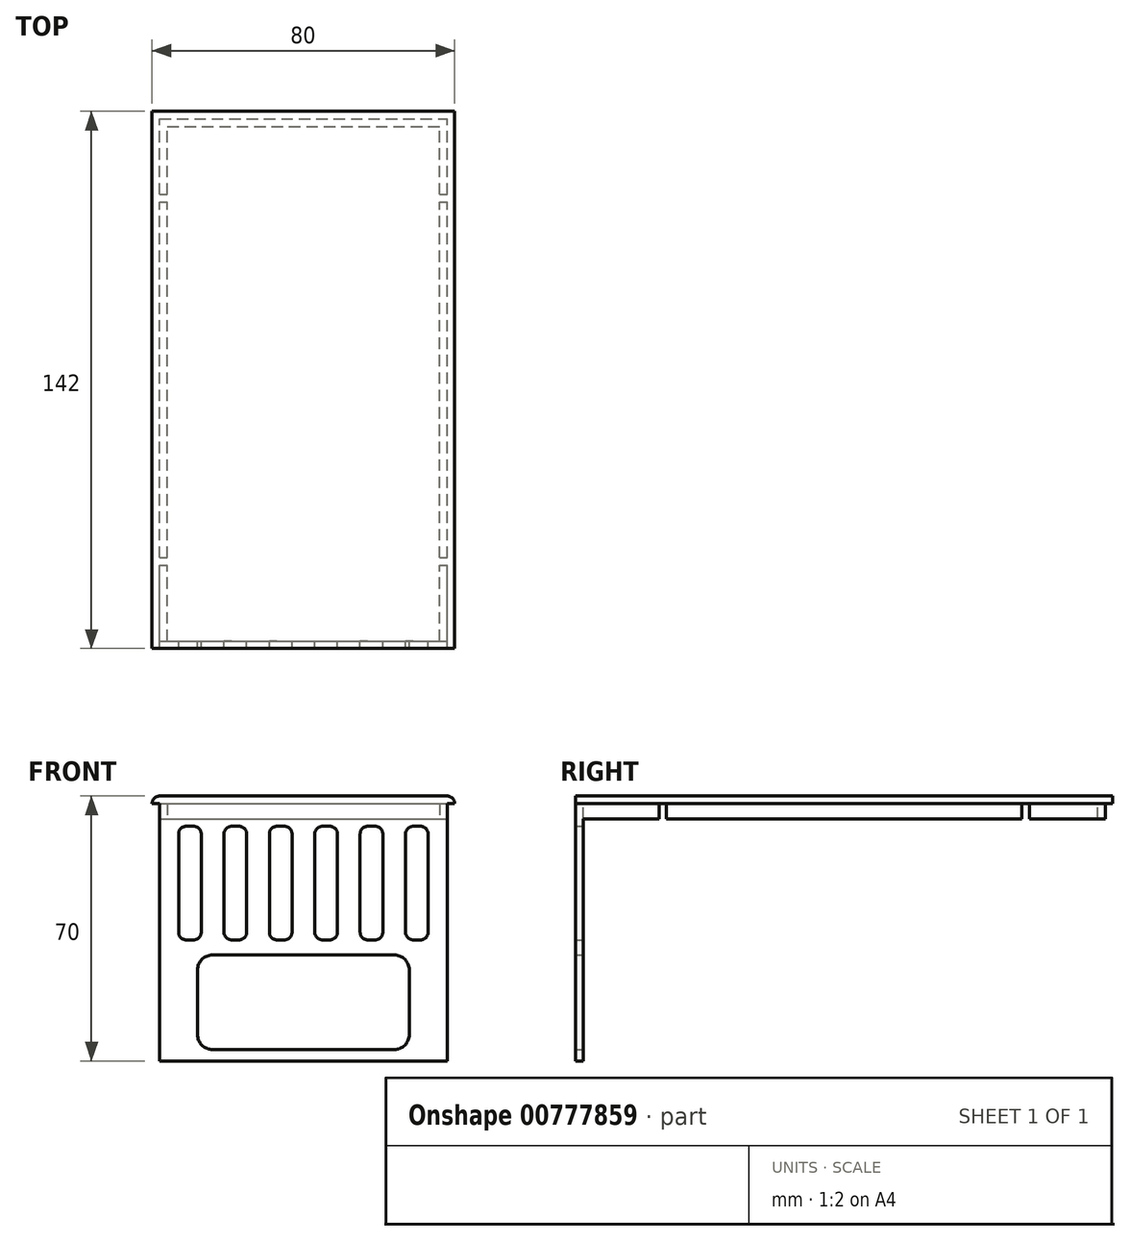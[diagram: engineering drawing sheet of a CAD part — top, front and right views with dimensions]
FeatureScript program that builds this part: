
annotation { "Feature Type Name" : "Feature", "Feature Type Description" : "" }
export const myFeature = defineFeature(function(context is Context, id is Id, definition is map)
    precondition{}
    {
        {
            var Q0;
            Q0=qCreatedBy(makeId("Front.planeOp"),FACE);
            var sketch = newSketch(context, id + "F0", { "sketchPlane" : qUnion([Q0])});
            skLineSegment(sketch, "E0.bottom", {"start": v(-40, -35) * mm, "end": v(36, -35) * mm});
            skLineSegment(sketch, "E0.top", {"start": v(-40, 33) * mm, "end": v(36, 33) * mm});
            skLineSegment(sketch, "E0.left", {"start": v(-40, -35) * mm, "end": v(-40, 33) * mm});
            skLineSegment(sketch, "E0.right", {"start": v(36, -35) * mm, "end": v(36, 33) * mm});
            skPoint(sketch, "E0.middle", {"position": v(-2, -1) * mm});
            skLineSegment(sketch, "E1.bottom", {"start": v(-30, -32) * mm, "end": v(26, -32) * mm});
            skLineSegment(sketch, "E1.top", {"start": v(-30, -7) * mm, "end": v(26, -7) * mm});
            skLineSegment(sketch, "E1.left", {"start": v(-30, -32) * mm, "end": v(-30, -7) * mm});
            skLineSegment(sketch, "E1.right", {"start": v(26, -32) * mm, "end": v(26, -7) * mm});
            skLineSegment(sketch, "E2.bottom", {"start": v(-35, -3) * mm, "end": v(-29, -3) * mm});
            skLineSegment(sketch, "E2.top", {"start": v(-35, 27) * mm, "end": v(-29, 27) * mm});
            skLineSegment(sketch, "E2.left", {"start": v(-35, -3) * mm, "end": v(-35, 27) * mm});
            skLineSegment(sketch, "E2.right", {"start": v(31, -3) * mm, "end": v(31, 27) * mm});
            skLineSegment(sketch, "E3", {"start": v(-29, 27) * mm, "end": v(-29, -3) * mm});
            skLineSegment(sketch, "E4", {"start": v(-23, 27) * mm, "end": v(-23, -3) * mm});
            skLineSegment(sketch, "E5", {"start": v(-17, 27) * mm, "end": v(-17, -3) * mm});
            skLineSegment(sketch, "E6", {"start": v(-11, 27) * mm, "end": v(-11, -3) * mm});
            skLineSegment(sketch, "E7", {"start": v(-5, 27) * mm, "end": v(-5, -3) * mm});
            skLineSegment(sketch, "E8", {"start": v(1, 27) * mm, "end": v(1, -3) * mm});
            skLineSegment(sketch, "E9", {"start": v(7, 27) * mm, "end": v(7, -3) * mm});
            skLineSegment(sketch, "E10", {"start": v(13, 27) * mm, "end": v(13, -3) * mm});
            skLineSegment(sketch, "E11", {"start": v(19, 27) * mm, "end": v(19, -3) * mm});
            skLineSegment(sketch, "E12", {"start": v(25, 27) * mm, "end": v(25, -3) * mm});
            skLineSegment(sketch, "E13", {"start": v(31, 27) * mm, "end": v(31, -3) * mm});
            skLineSegment(sketch, "E14.trimOffspring", {"start": v(-23, 27) * mm, "end": v(-17, 27) * mm});
            skLineSegment(sketch, "E15.trimOffspring", {"start": v(-23, -3) * mm, "end": v(-17, -3) * mm});
            skLineSegment(sketch, "E16.trimOffspring", {"start": v(-11, 27) * mm, "end": v(-5, 27) * mm});
            skLineSegment(sketch, "E17.trimOffspring", {"start": v(-11, -3) * mm, "end": v(-5, -3) * mm});
            skLineSegment(sketch, "E18.trimOffspring", {"start": v(1, -3) * mm, "end": v(7, -3) * mm});
            skLineSegment(sketch, "E19.trimOffspring", {"start": v(1, 27) * mm, "end": v(7, 27) * mm});
            skLineSegment(sketch, "E20.trimOffspring", {"start": v(13, 27) * mm, "end": v(19, 27) * mm});
            skLineSegment(sketch, "E21.trimOffspring", {"start": v(13, -3) * mm, "end": v(19, -3) * mm});
            skLineSegment(sketch, "E22.trimOffspring", {"start": v(25, 27) * mm, "end": v(31, 27) * mm});
            skLineSegment(sketch, "E23.trimOffspring", {"start": v(25, -3) * mm, "end": v(31, -3) * mm});
            skSolve(sketch);
        }
        {
            var Q0;
            Q0=makeQuery(id+"F0.imprint","IMPRINT",FACE,{"disambiguationData":[TD([[makeQuery(id+"F0.imprint","IMPRINT",EDGE,{"derivedFrom":sQuery(id+"F0.wireOp",EDGE,"E0.bottom")}),1.0]])]});
            extrude(context, id + "F1", {"entities" : qUnion([Q0]), "depth" : 2 * mm, "offsetDistance" : 25 * mm});
        }
        {
            var Q0;
            Q0=makeQuery(id+"F1.opExtrude","SWEPT_FACE",FACE,{"disambiguationData":[OSD([sQuery(id+"F0.wireOp",EDGE,"E0.top")])]});
            var sketch = newSketch(context, id + "F2", { "sketchPlane" : qUnion([Q0])});
            skLineSegment(sketch, "E24.bottom", {"start": v(-42, -2) * mm, "end": v(38, -2) * mm});
            skLineSegment(sketch, "E24.top", {"start": v(-42, 140) * mm, "end": v(38, 140) * mm});
            skLineSegment(sketch, "E24.left", {"start": v(-42, -2) * mm, "end": v(-42, 140) * mm});
            skLineSegment(sketch, "E24.right", {"start": v(38, -2) * mm, "end": v(38, 140) * mm});
            skSolve(sketch);
        }
        {
            var Q0;
            Q0 = qSketchRegion(id + "F2", true);
            extrude(context, id + "F3", {"entities" : qUnion([Q0]), "operationType" : NewBodyOperationType.ADD, "depth" : 2 * mm, "offsetDistance" : 25 * mm});
        }
        {
            var Q0;
            Q0=makeQuery(id+"F3.opExtrude","CAP_EDGE",EDGE,{"disambiguationData":[OSD([sQuery(id+"F2.wireOp",EDGE,"E24.right")])],"isStart":false});
            var Q1;
            Q1=makeQuery(id+"F3.opExtrude","CAP_EDGE",EDGE,{"disambiguationData":[OSD([sQuery(id+"F2.wireOp",EDGE,"E24.left")])],"isStart":false});
            fillet(context, id + "F4", {"entities" : qUnion([Q0, Q1]), "radius" : 2 * mm, "tangentPropagation" : true, "allowEdgeOverflow" : false});
        }
        {
            var Q0;
            Q0=makeQuery(id+"F3.opExtrude","CAP_FACE",FACE,{"disambiguationData":[OSD([sQuery(id+"F2.wireOp",EDGE,"E24.bottom"),sQuery(id+"F2.wireOp",EDGE,"E24.top"),sQuery(id+"F2.wireOp",EDGE,"E24.left"),sQuery(id+"F2.wireOp",EDGE,"E24.right")])],"isStart":true});
            var sketch = newSketch(context, id + "F5", { "sketchPlane" : qUnion([Q0])});
            skLineSegment(sketch, "E25.bottom", {"start": v(-40, 0) * mm, "end": v(36, 0) * mm});
            skLineSegment(sketch, "E25.top", {"start": v(-40, -138) * mm, "end": v(36, -138) * mm});
            skLineSegment(sketch, "E25.left", {"start": v(-40, 0) * mm, "end": v(-40, -138) * mm});
            skLineSegment(sketch, "E25.right", {"start": v(36, 0) * mm, "end": v(36, -138) * mm});
            skLineSegment(sketch, "E26.bottom", {"start": v(-38, 0) * mm, "end": v(34, 0) * mm});
            skLineSegment(sketch, "E26.top", {"start": v(-38, -136) * mm, "end": v(34, -136) * mm});
            skLineSegment(sketch, "E26.left", {"start": v(-38, 0) * mm, "end": v(-38, -136) * mm});
            skLineSegment(sketch, "E26.right", {"start": v(34, 0) * mm, "end": v(34, -136) * mm});
            skSolve(sketch);
        }
        {
            var Q0;
            Q0=makeQuery(id+"F5.imprint","IMPRINT",FACE,{"disambiguationData":[TD([[makeQuery(id+"F5.imprint","IMPRINT",EDGE,{"derivedFrom":sQuery(id+"F5.wireOp",EDGE,"E25.top")}),1.0]])]});
            extrude(context, id + "F6", {"entities" : qUnion([Q0]), "operationType" : NewBodyOperationType.ADD, "depth" : 4 * mm, "offsetDistance" : 25 * mm});
        }
        {
            var Q0;
            Q0=makeQuery(id+"F1.opExtrude","SWEPT_EDGE",EDGE,{"disambiguationData":[OSD([sQuery(id+"F0.wireOp",EDGE,"E1.top"),sQuery(id+"F0.wireOp",EDGE,"E1.left")])]});
            var Q1;
            Q1=makeQuery(id+"F1.opExtrude","SWEPT_EDGE",EDGE,{"disambiguationData":[OSD([sQuery(id+"F0.wireOp",EDGE,"E1.top"),sQuery(id+"F0.wireOp",EDGE,"E1.right")])]});
            var Q2;
            Q2=makeQuery(id+"F1.opExtrude","SWEPT_EDGE",EDGE,{"disambiguationData":[OSD([sQuery(id+"F0.wireOp",EDGE,"E1.bottom"),sQuery(id+"F0.wireOp",EDGE,"E1.left")])]});
            var Q3;
            Q3=makeQuery(id+"F1.opExtrude","SWEPT_EDGE",EDGE,{"disambiguationData":[OSD([sQuery(id+"F0.wireOp",EDGE,"E1.bottom"),sQuery(id+"F0.wireOp",EDGE,"E1.right")])]});
            fillet(context, id + "F7", {"entities" : qUnion([Q0, Q1, Q2, Q3]), "radius" : 4 * mm, "tangentPropagation" : true, "allowEdgeOverflow" : false});
        }
        {
            var Q0;
            Q0=makeQuery(id+"F1.opExtrude","SWEPT_EDGE",EDGE,{"disambiguationData":[OSD([sQuery(id+"F0.wireOp",EDGE,"E2.top"),sQuery(id+"F0.wireOp",EDGE,"E2.left")])]});
            var Q1;
            Q1=makeQuery(id+"F1.opExtrude","SWEPT_EDGE",EDGE,{"disambiguationData":[OSD([sQuery(id+"F0.wireOp",EDGE,"E2.top"),sQuery(id+"F0.wireOp",EDGE,"E3")])]});
            var Q2;
            Q2=makeQuery(id+"F1.opExtrude","SWEPT_EDGE",EDGE,{"disambiguationData":[OSD([sQuery(id+"F0.wireOp",EDGE,"E2.bottom"),sQuery(id+"F0.wireOp",EDGE,"E2.left")])]});
            var Q3;
            Q3=makeQuery(id+"F1.opExtrude","SWEPT_EDGE",EDGE,{"disambiguationData":[OSD([sQuery(id+"F0.wireOp",EDGE,"E2.bottom"),sQuery(id+"F0.wireOp",EDGE,"E3")])]});
            var Q4;
            Q4=makeQuery(id+"F1.opExtrude","SWEPT_EDGE",EDGE,{"disambiguationData":[OSD([sQuery(id+"F0.wireOp",EDGE,"E4"),sQuery(id+"F0.wireOp",EDGE,"E14.trimOffspring")])]});
            var Q5;
            Q5=makeQuery(id+"F1.opExtrude","SWEPT_EDGE",EDGE,{"disambiguationData":[OSD([sQuery(id+"F0.wireOp",EDGE,"E5"),sQuery(id+"F0.wireOp",EDGE,"E14.trimOffspring")])]});
            var Q6;
            Q6=makeQuery(id+"F1.opExtrude","SWEPT_EDGE",EDGE,{"disambiguationData":[OSD([sQuery(id+"F0.wireOp",EDGE,"E4"),sQuery(id+"F0.wireOp",EDGE,"E15.trimOffspring")])]});
            var Q7;
            Q7=makeQuery(id+"F1.opExtrude","SWEPT_EDGE",EDGE,{"disambiguationData":[OSD([sQuery(id+"F0.wireOp",EDGE,"E5"),sQuery(id+"F0.wireOp",EDGE,"E15.trimOffspring")])]});
            var Q8;
            Q8=makeQuery(id+"F1.opExtrude","SWEPT_EDGE",EDGE,{"disambiguationData":[OSD([sQuery(id+"F0.wireOp",EDGE,"E6"),sQuery(id+"F0.wireOp",EDGE,"E17.trimOffspring")])]});
            var Q9;
            Q9=makeQuery(id+"F1.opExtrude","SWEPT_EDGE",EDGE,{"disambiguationData":[OSD([sQuery(id+"F0.wireOp",EDGE,"E6"),sQuery(id+"F0.wireOp",EDGE,"E16.trimOffspring")])]});
            var Q10;
            Q10=makeQuery(id+"F1.opExtrude","SWEPT_EDGE",EDGE,{"disambiguationData":[OSD([sQuery(id+"F0.wireOp",EDGE,"E7"),sQuery(id+"F0.wireOp",EDGE,"E16.trimOffspring")])]});
            var Q11;
            Q11=makeQuery(id+"F1.opExtrude","SWEPT_EDGE",EDGE,{"disambiguationData":[OSD([sQuery(id+"F0.wireOp",EDGE,"E7"),sQuery(id+"F0.wireOp",EDGE,"E17.trimOffspring")])]});
            var Q12;
            Q12=makeQuery(id+"F1.opExtrude","SWEPT_EDGE",EDGE,{"disambiguationData":[OSD([sQuery(id+"F0.wireOp",EDGE,"E8"),sQuery(id+"F0.wireOp",EDGE,"E18.trimOffspring")])]});
            var Q13;
            Q13=makeQuery(id+"F1.opExtrude","SWEPT_EDGE",EDGE,{"disambiguationData":[OSD([sQuery(id+"F0.wireOp",EDGE,"E9"),sQuery(id+"F0.wireOp",EDGE,"E18.trimOffspring")])]});
            var Q14;
            Q14=makeQuery(id+"F1.opExtrude","SWEPT_EDGE",EDGE,{"disambiguationData":[OSD([sQuery(id+"F0.wireOp",EDGE,"E9"),sQuery(id+"F0.wireOp",EDGE,"E19.trimOffspring")])]});
            var Q15;
            Q15=makeQuery(id+"F1.opExtrude","SWEPT_EDGE",EDGE,{"disambiguationData":[OSD([sQuery(id+"F0.wireOp",EDGE,"E8"),sQuery(id+"F0.wireOp",EDGE,"E19.trimOffspring")])]});
            var Q16;
            Q16=makeQuery(id+"F1.opExtrude","SWEPT_EDGE",EDGE,{"disambiguationData":[OSD([sQuery(id+"F0.wireOp",EDGE,"E10"),sQuery(id+"F0.wireOp",EDGE,"E20.trimOffspring")])]});
            var Q17;
            Q17=makeQuery(id+"F1.opExtrude","SWEPT_EDGE",EDGE,{"disambiguationData":[OSD([sQuery(id+"F0.wireOp",EDGE,"E11"),sQuery(id+"F0.wireOp",EDGE,"E20.trimOffspring")])]});
            var Q18;
            Q18=makeQuery(id+"F1.opExtrude","SWEPT_EDGE",EDGE,{"disambiguationData":[OSD([sQuery(id+"F0.wireOp",EDGE,"E11"),sQuery(id+"F0.wireOp",EDGE,"E21.trimOffspring")])]});
            var Q19;
            Q19=makeQuery(id+"F1.opExtrude","SWEPT_EDGE",EDGE,{"disambiguationData":[OSD([sQuery(id+"F0.wireOp",EDGE,"E10"),sQuery(id+"F0.wireOp",EDGE,"E21.trimOffspring")])]});
            var Q20;
            Q20=makeQuery(id+"F1.opExtrude","SWEPT_EDGE",EDGE,{"disambiguationData":[OSD([sQuery(id+"F0.wireOp",EDGE,"E12"),sQuery(id+"F0.wireOp",EDGE,"E23.trimOffspring")])]});
            var Q21;
            Q21=makeQuery(id+"F1.opExtrude","SWEPT_EDGE",EDGE,{"disambiguationData":[OSD([sQuery(id+"F0.wireOp",EDGE,"E13"),sQuery(id+"F0.wireOp",EDGE,"E23.trimOffspring")])]});
            var Q22;
            Q22=makeQuery(id+"F1.opExtrude","SWEPT_EDGE",EDGE,{"disambiguationData":[OSD([sQuery(id+"F0.wireOp",EDGE,"E12"),sQuery(id+"F0.wireOp",EDGE,"E22.trimOffspring")])]});
            var Q23;
            Q23=makeQuery(id+"F1.opExtrude","SWEPT_EDGE",EDGE,{"disambiguationData":[OSD([sQuery(id+"F0.wireOp",EDGE,"E13"),sQuery(id+"F0.wireOp",EDGE,"E22.trimOffspring")])]});
            fillet(context, id + "F8", {"entities" : qUnion([Q0, Q1, Q2, Q3, Q4, Q5, Q6, Q7, Q8, Q9, Q10, Q11, Q12, Q13, Q14, Q15, Q16, Q17, Q18, Q19, Q20, Q21, Q22, Q23]), "radius" : 2 * mm, "tangentPropagation" : true, "allowEdgeOverflow" : false});
        }
        {
            var Q0;
            Q0=makeQuery(id+"F6.boolean.opBoolean","MERGE",FACE,{"derivedFrom":[makeQuery(id+"F1.opExtrude","SWEPT_FACE",FACE,{"disambiguationData":[OSD([sQuery(id+"F0.wireOp",EDGE,"E0.left")])]}),makeQuery(id+"F6.opExtrude","SWEPT_FACE",FACE,{"disambiguationData":[OSD([sQuery(id+"F5.wireOp",EDGE,"E25.left")])]})]});
            var sketch = newSketch(context, id + "F9", { "sketchPlane" : qUnion([Q0])});
            skLineSegment(sketch, "E27.bottom", {"start": v(-118, 33) * mm, "end": v(-116, 33) * mm});
            skLineSegment(sketch, "E27.top", {"start": v(-118, 29) * mm, "end": v(-116, 29) * mm});
            skLineSegment(sketch, "E27.left", {"start": v(-118, 33) * mm, "end": v(-118, 29) * mm});
            skLineSegment(sketch, "E27.right", {"start": v(-116, 33) * mm, "end": v(-116, 29) * mm});
            skLineSegment(sketch, "E28.bottom", {"start": v(-22, 33) * mm, "end": v(-20, 33) * mm});
            skLineSegment(sketch, "E28.top", {"start": v(-22, 29) * mm, "end": v(-20, 29) * mm});
            skLineSegment(sketch, "E28.left", {"start": v(-22, 33) * mm, "end": v(-22, 29) * mm});
            skLineSegment(sketch, "E28.right", {"start": v(-20, 33) * mm, "end": v(-20, 29) * mm});
            skSolve(sketch);
        }
        {
            var Q0;
            Q0=makeQuery(id+"F9.imprint","IMPRINT",FACE,{"disambiguationData":[TD([[makeQuery(id+"F9.imprint","IMPRINT",EDGE,{"derivedFrom":sQuery(id+"F9.wireOp",EDGE,"E27.bottom")}),1.0]])]});
            var Q1;
            Q1=makeQuery(id+"F9.imprint","IMPRINT",FACE,{"disambiguationData":[TD([[makeQuery(id+"F9.imprint","IMPRINT",EDGE,{"derivedFrom":sQuery(id+"F9.wireOp",EDGE,"E28.bottom")}),1.0]])]});
            extrude(context, id + "F10", {"entities" : qUnion([Q0, Q1]), "operationType" : NewBodyOperationType.REMOVE, "depth" : 200 * mm, "offsetDistance" : 25 * mm, "symmetric" : true});
        }
    });
